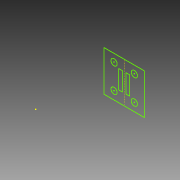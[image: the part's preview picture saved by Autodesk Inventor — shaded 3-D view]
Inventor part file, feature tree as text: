
AUTODESK INVENTOR PART (.ipt)
format: ipt  version: 2015 (Build 190159000, 159)  size: 61,440 bytes
history: native  units: in
note: dims shown in document units (in); Inventor stores cm internally (conversion verified against a paired STEP export)
features: sketch x1
ambient origin geometry x8: Origin, YZ Plane, XZ Plane, XY Plane, X Axis, Y Axis, Z Axis, Center Point
feature tree (1):
  sketch  "Sketch1"
